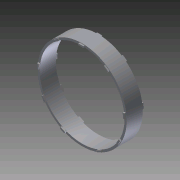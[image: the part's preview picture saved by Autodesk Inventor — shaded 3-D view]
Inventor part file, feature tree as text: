
AUTODESK INVENTOR PART (.ipt)
format: ipt  version: 2011 (Build 150239000, 239)  size: 201,216 bytes
history: native  units: in
note: dims shown in document units (in); Inventor stores cm internally (conversion verified against a paired STEP export)
features: projected_geometry x7, extrude x3, sketch x3
ambient origin geometry x8: Origin, YZ Plane, XZ Plane, XY Plane, X Axis, Y Axis, Z Axis, Center Point
bodies: Solid1 (feature_tree)
feature tree (13):
  extrude  "Extrusion1"  Depth=5.277in
  extrude  "Extrusion2"  Depth=0.103in
  extrude  "Extrusion3"  Depth=0.7874in
  sketch  "Sketch1"  dims[d0=5.55in d1=5.277in]
  sketch  "Sketch2"  dims[d2=1.0in d3=0.0in d4=0.103in]
  sketch  "Sketch3"  dims[d5=0.32in d6=0.7874in d8=0.2405in d10=0.7874in d12=0.2405in d14=0.7874in d16=0.3436in d18=1.1811in d20=0.481in d22=0.7874in d24=0.3436in d26=0.7874in d28=0.3436in d30=1.1811in d32=0.481in d34=0.088in d35=0.0in d36=0.088in d37=0.0in]
  projected_geometry  "Projected Loop1"
  projected_geometry  "Projected Loop2"
  projected_geometry  "Projected Loop3"
  projected_geometry  "Projected Loop4"
  projected_geometry  "Projected Loop5"
  projected_geometry  "Projected Loop6"
  projected_geometry  "Projected Loop7"
